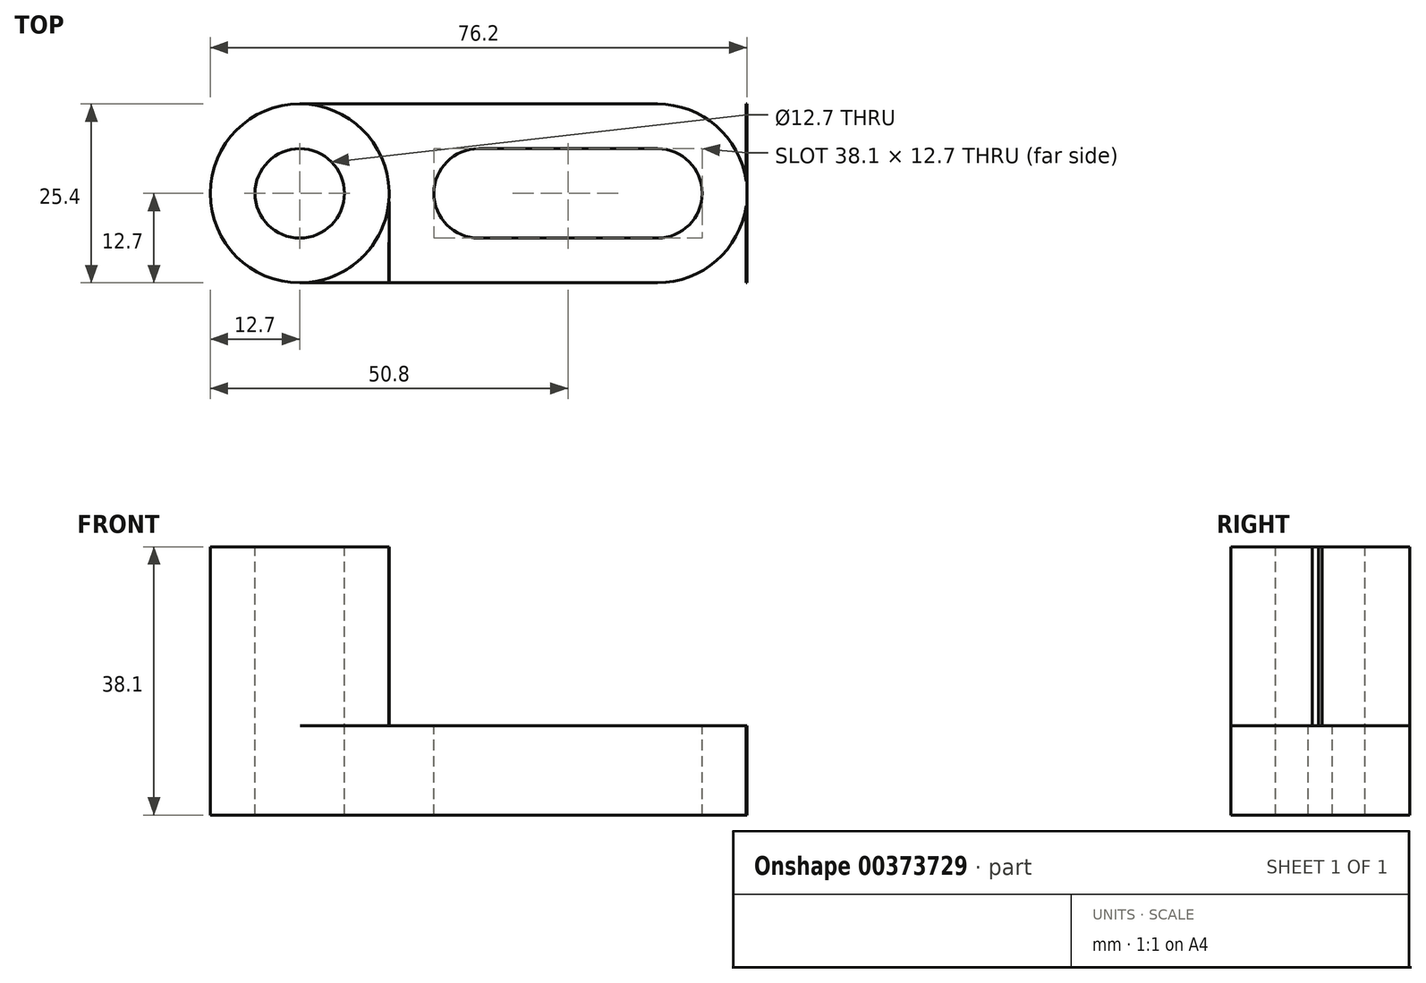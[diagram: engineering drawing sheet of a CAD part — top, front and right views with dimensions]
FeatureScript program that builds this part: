
annotation { "Feature Type Name" : "Feature", "Feature Type Description" : "" }
export const myFeature = defineFeature(function(context is Context, id is Id, definition is map)
    precondition{}
    {
        {
            var Q0;
            Q0=qCreatedBy(makeId("Front.planeOp"),FACE);
            var sketch = newSketch(context, id + "F0", { "sketchPlane" : qUnion([Q0])});
            skLineSegment(sketch, "E0.bottom", {"start": v(0, 0) * mm, "end": v(76.2, 0) * mm});
            skLineSegment(sketch, "E0.top", {"start": v(0, 12.7) * mm, "end": v(76.2, 12.7) * mm});
            skLineSegment(sketch, "E0.left", {"start": v(0, 0) * mm, "end": v(0, 12.7) * mm});
            skLineSegment(sketch, "E0.right", {"start": v(76.2, 0) * mm, "end": v(76.2, 12.7) * mm});
            skLineSegment(sketch, "E1.bottom", {"start": v(0, 0) * mm, "end": v(25.4, 0) * mm});
            skLineSegment(sketch, "E1.top", {"start": v(0, 38.1) * mm, "end": v(25.4, 38.1) * mm});
            skLineSegment(sketch, "E1.left", {"start": v(0, 0) * mm, "end": v(0, 38.1) * mm});
            skLineSegment(sketch, "E1.right", {"start": v(25.4, 0) * mm, "end": v(25.4, 38.1) * mm});
            skSolve(sketch);
        }
        {
            var Q0;
            {var subQ5=sQuery(id+"F0.wireOp",EDGE,"E1.top");Q0=makeQuery(id+"F0.imprint","IMPRINT",FACE,{"disambiguationData":[TD([[makeQuery(id+"F0.imprint","IMPRINT",EDGE,{"derivedFrom":subQ5}),-1.0]])]});}
            var Q1;
            {var subQ5=sQuery(id+"F0.wireOp",EDGE,"E1.bottom");Q1=makeQuery(id+"F0.imprint","IMPRINT",FACE,{"disambiguationData":[TD([[makeQuery(id+"F0.imprint","IMPRINT",EDGE,{"derivedFrom":subQ5}),1.0]])]});}
            var Q2;
            {var subQ0=sQuery(id+"F0.wireOp",EDGE,"E0.bottom");Q2=makeQuery(id+"F0.imprint","IMPRINT",FACE,{"disambiguationData":[TD([[makeQuery(id+"F0.imprint","IMPRINT",EDGE,{"derivedFrom":subQ0}),1.0]])]});}
            extrude(context, id + "F1", {"entities" : qUnion([Q0, Q1, Q2]), "depth" : 25.4 * mm});
        }
        {
            var Q0;
            Q0=makeQuery(id+"F1.opExtrude","SWEPT_FACE",FACE,{"disambiguationData":[OSD([sQuery(id+"F0.wireOp",EDGE,"E1.top")])]});
            var sketch = newSketch(context, id + "F2", { "sketchPlane" : qUnion([Q0])});
            skCircle(sketch, "E2", {"center": v(12.7, -12.7) * mm, "radius": 6.35 * mm});
            skPoint(sketch, "E2.centerSnap0", {"position": v(12.7, 0) * mm});
            skCircle(sketch, "E3", {"center": v(12.7, -12.7) * mm, "radius": 12.7 * mm});
            skCircle(sketch, "E4", {"center": v(38.1, -12.7) * mm, "radius": 6.35 * mm});
            skPoint(sketch, "E4.centerSnap0", {"position": v(25.4, -12.7) * mm});
            skCircle(sketch, "E5", {"center": v(63.5, -12.7) * mm, "radius": 6.35 * mm});
            skLineSegment(sketch, "E6", {"start": v(38.1, -6.35) * mm, "end": v(63.5, -6.35) * mm});
            skLineSegment(sketch, "E7", {"start": v(38.1, -19.05) * mm, "end": v(63.5, -19.05) * mm});
            skArc(sketch, "E8", {"start": v(63.5, -25.4) * mm, "mid": v(76.2, -12.7) * mm, "end": v(63.5, 0) * mm});
            skLineSegment(sketch, "E9", {"start": v(63.5, -25.4) * mm, "end": v(63.5, -25.4) * mm});
            skLineSegment(sketch, "E10", {"start": v(63.5, -25.4) * mm, "end": v(76.08, -25.4) * mm});
            skLineSegment(sketch, "E11", {"start": v(76.08, -25.4) * mm, "end": v(76.08, 0) * mm});
            skLineSegment(sketch, "E12", {"start": v(76.08, 0) * mm, "end": v(63.5, 0) * mm});
            skSolve(sketch);
        }
        {
            var Q0;
            {var subQ0=sQuery(id+"F2.wireOp",EDGE,"E3");var subQ1=sQuery(id+"F0.wireOp",EDGE,"E1.top");var subQ2=makeQuery(id+"F1.opExtrude","CAP_EDGE",EDGE,{"disambiguationData":[OSD([subQ1])],"isStart":true});var subQ3=makeQuery(id+"F2.imprint","INTERSECT",VERTEX,{"derivedFrom":[subQ2,subQ0]});Q0=makeQuery(id+"F2.imprint","IMPRINT",FACE,{"disambiguationData":[TD([[makeQuery(id+"F2.imprint","IMPRINT",EDGE,{"disambiguationData":[TD([[subQ3,1.0]])],"derivedFrom":subQ0}),-1.0]])]});}
            var sketch = newSketch(context, id + "F3", { "sketchPlane" : qUnion([Q0])});
            skArc(sketch, "E13", {"start": v(12.64, -25.4) * mm, "mid": v(25.4, -12.76) * mm, "end": v(12.76, 0) * mm});
            skLineSegment(sketch, "E14", {"start": v(12.64, -25.4) * mm, "end": v(25.37, -25.46) * mm});
            skLineSegment(sketch, "E15", {"start": v(25.37, -25.46) * mm, "end": v(25.4, -12.74) * mm});
            skSolve(sketch);
        }
        {
            var Q0;
            {var subQ0=sQuery(id+"F2.wireOp",EDGE,"E3");var subQ1=sQuery(id+"F0.wireOp",EDGE,"E1.top");var subQ4=makeQuery(id+"F1.opExtrude","CAP_EDGE",EDGE,{"disambiguationData":[OSD([subQ1])],"isStart":false});var subQ5=makeQuery(id+"F2.imprint","INTERSECT",VERTEX,{"derivedFrom":[subQ4,subQ0]});Q0=makeQuery(id+"F2.imprint","IMPRINT",FACE,{"disambiguationData":[TD([[makeQuery(id+"F2.imprint","IMPRINT",EDGE,{"disambiguationData":[TD([[subQ5,1.0]])],"derivedFrom":subQ0}),-1.0]])]});}
            var Q1;
            {var subQ0=sQuery(id+"F2.wireOp",EDGE,"E3");var subQ1=sQuery(id+"F0.wireOp",EDGE,"E1.top");var subQ2=makeQuery(id+"F1.opExtrude","CAP_EDGE",EDGE,{"disambiguationData":[OSD([subQ1])],"isStart":true});var subQ3=makeQuery(id+"F2.imprint","INTERSECT",VERTEX,{"derivedFrom":[subQ2,subQ0]});Q1=makeQuery(id+"F2.imprint","IMPRINT",FACE,{"disambiguationData":[TD([[makeQuery(id+"F2.imprint","IMPRINT",EDGE,{"disambiguationData":[TD([[subQ3,-1.0]])],"derivedFrom":subQ0}),-1.0]])]});}
            var Q2;
            Q2=makeQuery(id+"F2.imprint","IMPRINT",FACE,{"disambiguationData":[TD([[makeQuery(id+"F2.imprint","IMPRINT",EDGE,{"derivedFrom":sQuery(id+"F2.wireOp",EDGE,"E2")}),1.0]])]});
            var Q3;
            {var subQ0=sQuery(id+"F2.wireOp",EDGE,"E4");var subQ1=makeQuery(id+"F2.imprint","INTERSECT",VERTEX,{"derivedFrom":[subQ0,sQuery(id+"F2.wireOp",EDGE,"E6")]});Q3=makeQuery(id+"F2.imprint","IMPRINT",FACE,{"disambiguationData":[TD([[makeQuery(id+"F2.imprint","IMPRINT",EDGE,{"disambiguationData":[TD([[subQ1,-1.0]])],"derivedFrom":subQ0}),1.0]])]});}
            var Q4;
            {var subQ0=sQuery(id+"F2.wireOp",EDGE,"E6");Q4=makeQuery(id+"F2.imprint","IMPRINT",FACE,{"disambiguationData":[TD([[makeQuery(id+"F2.imprint","IMPRINT",EDGE,{"derivedFrom":subQ0}),-1.0]])]});}
            var Q5;
            {var subQ0=sQuery(id+"F2.wireOp",EDGE,"E5");var subQ1=makeQuery(id+"F2.imprint","INTERSECT",VERTEX,{"derivedFrom":[subQ0,sQuery(id+"F2.wireOp",EDGE,"E6")]});Q5=makeQuery(id+"F2.imprint","IMPRINT",FACE,{"disambiguationData":[TD([[makeQuery(id+"F2.imprint","IMPRINT",EDGE,{"disambiguationData":[TD([[subQ1,-1.0]])],"derivedFrom":subQ0}),1.0]])]});}
            var Q6;
            {var subQ0=sQuery(id+"F2.wireOp",EDGE,"E10");Q6=makeQuery(id+"F2.imprint","IMPRINT",FACE,{"disambiguationData":[TD([[makeQuery(id+"F2.imprint","IMPRINT",EDGE,{"derivedFrom":subQ0}),1.0]])]});}
            var Q7;
            {var subQ0=sQuery(id+"F2.wireOp",EDGE,"E12");Q7=makeQuery(id+"F2.imprint","IMPRINT",FACE,{"disambiguationData":[TD([[makeQuery(id+"F2.imprint","IMPRINT",EDGE,{"derivedFrom":subQ0}),1.0]])]});}
            extrude(context, id + "F4", {"entities" : qUnion([Q0, Q1, Q2, Q3, Q4, Q5, Q6, Q7]), "operationType" : NewBodyOperationType.REMOVE, "oppositeDirection" : true, "depth" : 25400 * mm});
        }
        {
            var Q0;
            {var subQ0=sQuery(id+"F3.wireOp",EDGE,"E13");var subQ1=sQuery(id+"F0.wireOp",EDGE,"E1.top");var subQ2=makeQuery(id+"F1.opExtrude","CAP_EDGE",EDGE,{"disambiguationData":[OSD([subQ1])],"isStart":true});var subQ5=sQuery(id+"F2.wireOp",EDGE,"E3");var subQ6=makeQuery(id+"F2.imprint","IMPRINT",EDGE,{"disambiguationData":[TD([[makeQuery(id+"F2.imprint","INTERSECT",VERTEX,{"derivedFrom":[subQ2,subQ5]}),-1.0]])],"derivedFrom":subQ2});var subQ7=makeQuery(id+"F3.imprint","INTERSECT",VERTEX,{"derivedFrom":[subQ6,subQ0]});Q0=makeQuery(id+"F3.imprint","IMPRINT",FACE,{"disambiguationData":[TD([[makeQuery(id+"F3.imprint","IMPRINT",EDGE,{"disambiguationData":[TD([[subQ7,1.0]])],"derivedFrom":subQ0}),-1.0]])]});}
            var Q1;
            {var subQ0=sQuery(id+"F3.wireOp",EDGE,"E14");Q1=makeQuery(id+"F3.imprint","IMPRINT",FACE,{"disambiguationData":[TD([[makeQuery(id+"F3.imprint","IMPRINT",EDGE,{"derivedFrom":subQ0}),1.0]])]});}
            extrude(context, id + "F5", {"entities" : qUnion([Q0, Q1]), "operationType" : NewBodyOperationType.REMOVE, "oppositeDirection" : true, "depth" : 25.4 * mm});
        }
    });
